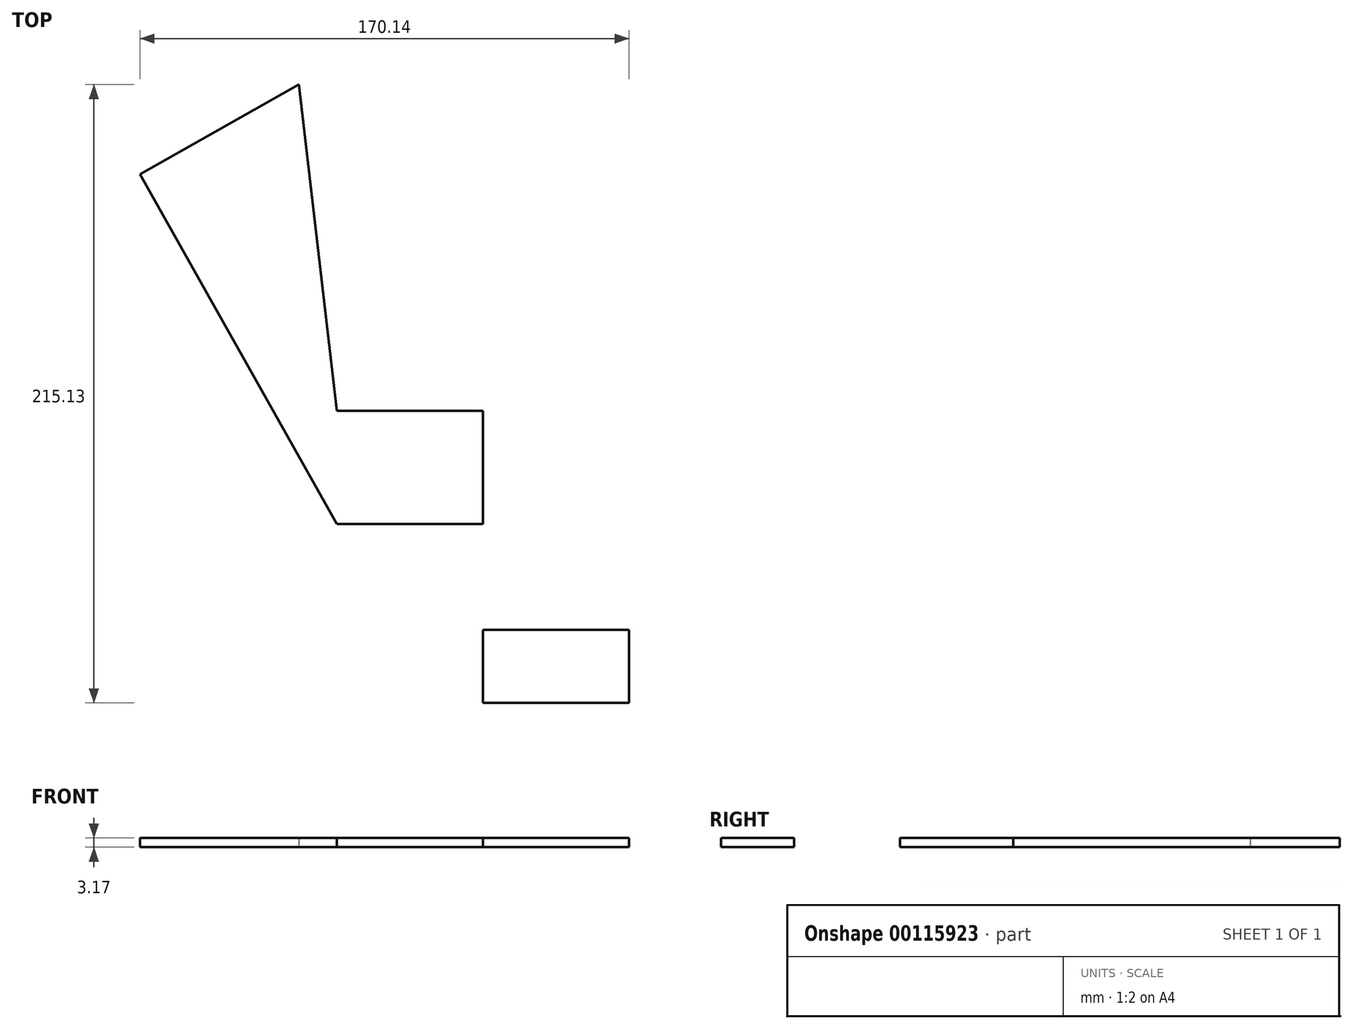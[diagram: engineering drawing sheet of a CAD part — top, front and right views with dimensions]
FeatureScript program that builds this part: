
annotation { "Feature Type Name" : "Feature", "Feature Type Description" : "" }
export const myFeature = defineFeature(function(context is Context, id is Id, definition is map)
    precondition{}
    {
        {
            var Q0;
            Q0=qCreatedBy(makeId("Top.planeOp"),FACE);
            var sketch = newSketch(context, id + "F0", { "sketchPlane" : qUnion([Q0])});
            skLineSegment(sketch, "E0.bottom", {"start": v(2.42, -8.43) * mm, "end": v(53.22, -8.43) * mm});
            skLineSegment(sketch, "E0.top", {"start": v(2.42, 16.97) * mm, "end": v(53.22, 16.97) * mm});
            skLineSegment(sketch, "E0.left", {"start": v(2.42, -8.43) * mm, "end": v(2.42, 16.97) * mm});
            skLineSegment(sketch, "E0.right", {"start": v(53.22, -8.43) * mm, "end": v(53.22, 16.97) * mm});
            skLineSegment(sketch, "E1.bottom", {"start": v(27.82, 16.97) * mm, "end": v(2.42, 16.97) * mm});
            skLineSegment(sketch, "E1.top", {"start": v(27.82, 16.97) * mm, "end": v(2.42, 16.97) * mm});
            skLineSegment(sketch, "E1.left", {"start": v(27.82, 16.97) * mm, "end": v(27.82, 16.97) * mm});
            skLineSegment(sketch, "E1.right", {"start": v(2.42, 16.97) * mm, "end": v(2.42, 16.97) * mm});
            skLineSegment(sketch, "E2.top", {"start": v(27.82, 93.17) * mm, "end": v(2.42, 93.17) * mm});
            skLineSegment(sketch, "E2.left", {"start": v(27.82, 16.97) * mm, "end": v(27.82, 93.17) * mm});
            skLineSegment(sketch, "E2.right", {"start": v(2.42, 16.97) * mm, "end": v(2.42, 93.17) * mm});
            skLineSegment(sketch, "E3.bottom", {"start": v(2.42, 93.17) * mm, "end": v(-48.38, 93.17) * mm});
            skLineSegment(sketch, "E3.top", {"start": v(2.42, 53.81) * mm, "end": v(-48.38, 53.81) * mm});
            skLineSegment(sketch, "E3.left", {"start": v(2.42, 93.17) * mm, "end": v(2.42, 53.81) * mm});
            skLineSegment(sketch, "E3.right", {"start": v(-48.38, 93.17) * mm, "end": v(-48.38, 53.81) * mm});
            skLineSegment(sketch, "E4", {"start": v(-48.38, 53.81) * mm, "end": v(-116.92, 175.55) * mm});
            skLineSegment(sketch, "E5", {"start": v(-116.92, 175.55) * mm, "end": v(-61.58, 206.7) * mm});
            skLineSegment(sketch, "E6", {"start": v(-61.58, 206.7) * mm, "end": v(-48.38, 93.17) * mm});
            skSolve(sketch);
        }
        {
            var Q0;
            Q0=makeQuery(id+"F0.imprint","IMPRINT",FACE,{"disambiguationData":[TD([[makeQuery(id+"F0.imprint","IMPRINT",EDGE,{"derivedFrom":sQuery(id+"F0.wireOp",EDGE,"E3.right")}),-1.0]])]});
            var Q1;
            Q1=makeQuery(id+"F0.imprint","IMPRINT",FACE,{"disambiguationData":[TD([[makeQuery(id+"F0.imprint","IMPRINT",EDGE,{"derivedFrom":sQuery(id+"F0.wireOp",EDGE,"E0.bottom")}),1.0]])]});
            var Q2;
            Q2=makeQuery(id+"F0.imprint","IMPRINT",FACE,{"disambiguationData":[TD([[makeQuery(id+"F0.imprint","IMPRINT",EDGE,{"derivedFrom":sQuery(id+"F0.wireOp",EDGE,"E1.bottom")}),-1.0]])]});
            var Q3;
            Q3=makeQuery(id+"F0.imprint","IMPRINT",FACE,{"disambiguationData":[TD([[makeQuery(id+"F0.imprint","IMPRINT",EDGE,{"derivedFrom":sQuery(id+"F0.wireOp",EDGE,"E3.bottom")}),1.0]])]});
            extrude(context, id + "F1", {"entities" : qUnion([Q0, Q1, Q2, Q3]), "depth" : 3.17 * mm});
        }
    });
